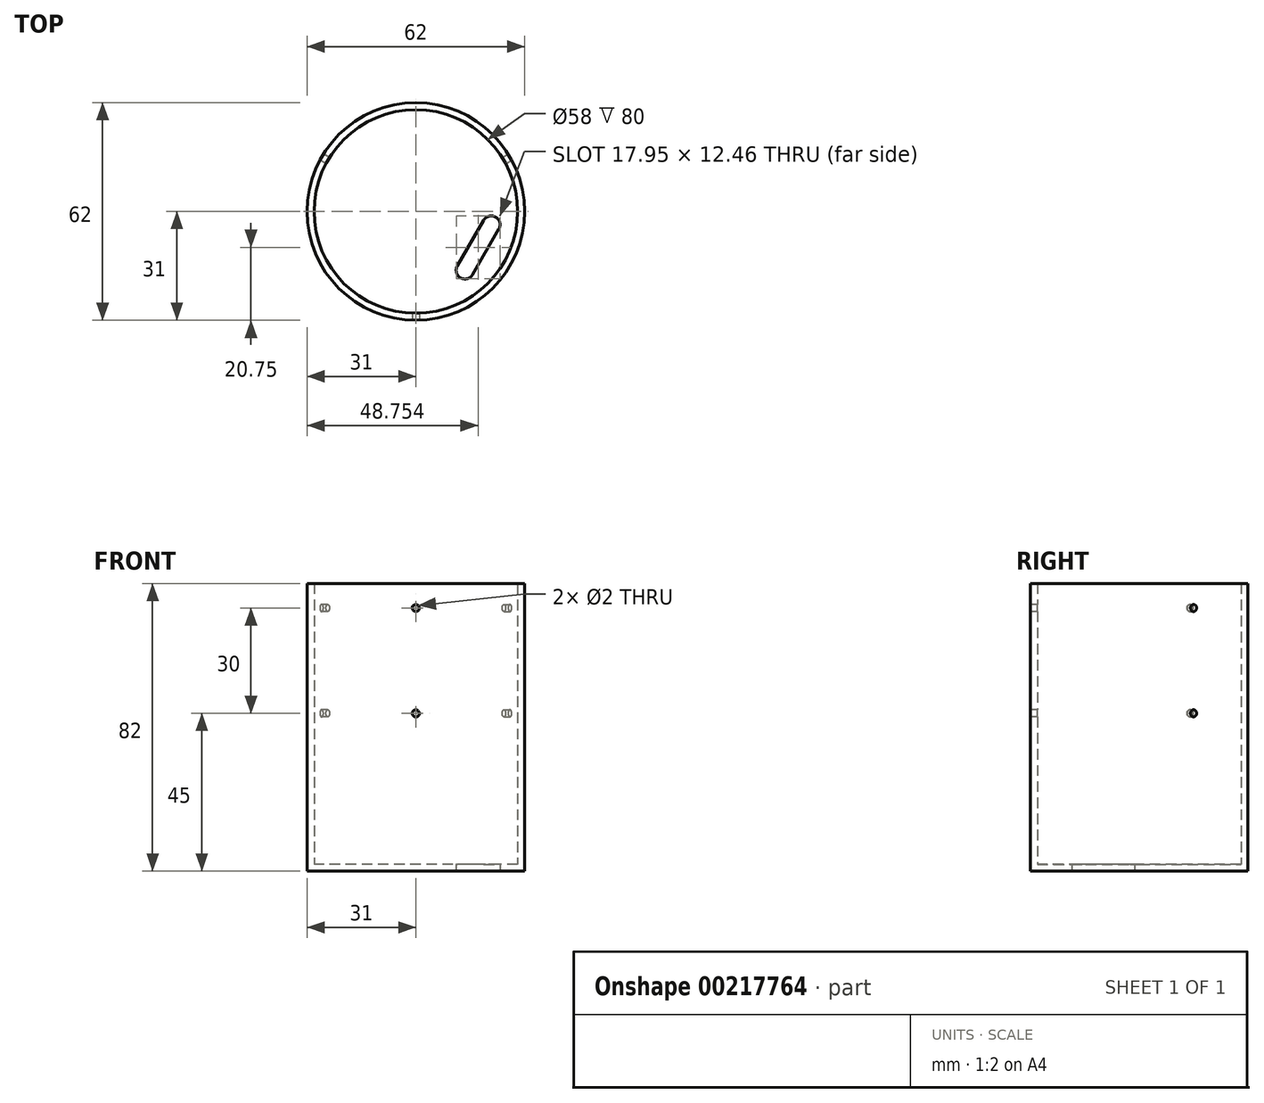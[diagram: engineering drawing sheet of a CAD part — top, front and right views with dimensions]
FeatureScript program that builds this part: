
annotation { "Feature Type Name" : "Feature", "Feature Type Description" : "" }
export const myFeature = defineFeature(function(context is Context, id is Id, definition is map)
    precondition{}
    {
        {
            var Q0;
            Q0=qCreatedBy(makeId("Top.planeOp"),FACE);
            var sketch = newSketch(context, id + "F0", { "sketchPlane" : qUnion([Q0])});
            skCircle(sketch, "E0", {"center": v(0, 0) * mm, "radius": 29 * mm});
            skCircle(sketch, "E1", {"center": v(0, 0) * mm, "radius": 31 * mm});
            skSolve(sketch);
        }
        {
            var Q0;
            Q0 = qSketchRegion(id + "F0", true);
            extrude(context, id + "F1", {"entities" : qUnion([Q0]), "depth" : 80 * mm});
        }
        {
            var Q0;
            Q0=qCreatedBy(makeId("Front.planeOp"),FACE);
            cPlane(context, id + "F2", {"entities" : qUnion([Q0]), "cplaneType" : CPlaneType.OFFSET, "offset" : 31 * mm, "width" : 150 * mm, "height" : 150 * mm});
        }
        {
            var Q0;
            Q0=qCreatedBy(id+"F2.planeOp",FACE);
            var sketch = newSketch(context, id + "F3", { "sketchPlane" : qUnion([Q0])});
            skLineSegment(sketch, "E2", {"start": v(0, 0) * mm, "end": v(0, 80) * mm, "construction": true});
            skCircle(sketch, "E3", {"center": v(0, 73) * mm, "radius": 1 * mm});
            skCircle(sketch, "E4", {"center": v(0, 43) * mm, "radius": 1 * mm});
            skSolve(sketch);
        }
        {
            var Q0;
            Q0 = qSketchRegion(id + "F3", true);
            extrude(context, id + "F4", {"entities" : qUnion([Q0]), "endBound" : BoundingType.UP_TO_NEXT, "oppositeDirection" : true, "depth" : 25 * mm});
        }
        {
            var Q0;
            Q0=makeQuery(id+"F4.opExtrude","SWEPT_BODY",BODY,{"disambiguationData":[OSD([sQuery(id+"F3.wireOp",EDGE,"E3")])]});
            var Q1;
            Q1=makeQuery(id+"F4.opExtrude","SWEPT_BODY",BODY,{"disambiguationData":[OSD([sQuery(id+"F3.wireOp",EDGE,"E4")])]});
            var Q2;
            Q2=makeQuery(id+"F1.opExtrude","CAP_EDGE",EDGE,{"disambiguationData":[OSD([sQuery(id+"F0.wireOp",EDGE,"E0")])],"isStart":false});
            circularPattern(context, id + "F5", {"entities" : qUnion([Q0, Q1]), "axis" : qUnion([Q2]), "angle" : 360 * degree, "instanceCount" : 3, "equalSpace" : true});
        }
        {
            var Q0;
            Q0=makeQuery(id+"F4.opExtrude","SWEPT_BODY",BODY,{"disambiguationData":[OSD([sQuery(id+"F3.wireOp",EDGE,"E3")])]});
            var Q1;
            Q1=makeQuery(id+"F4.opExtrude","SWEPT_BODY",BODY,{"disambiguationData":[OSD([sQuery(id+"F3.wireOp",EDGE,"E4")])]});
            var Q2;
            Q2=makeQuery(id+"F5.opPattern","COPY",BODY,{"derivedFrom":makeQuery(id+"F4.opExtrude","SWEPT_BODY",BODY,{"disambiguationData":[OSD([sQuery(id+"F3.wireOp",EDGE,"E3")])]}),"instanceName":"1"});
            var Q3;
            Q3=makeQuery(id+"F5.opPattern","COPY",BODY,{"derivedFrom":makeQuery(id+"F4.opExtrude","SWEPT_BODY",BODY,{"disambiguationData":[OSD([sQuery(id+"F3.wireOp",EDGE,"E4")])]}),"instanceName":"1"});
            var Q4;
            Q4=makeQuery(id+"F5.opPattern","COPY",BODY,{"derivedFrom":makeQuery(id+"F4.opExtrude","SWEPT_BODY",BODY,{"disambiguationData":[OSD([sQuery(id+"F3.wireOp",EDGE,"E3")])]}),"instanceName":"2"});
            var Q5;
            Q5=makeQuery(id+"F5.opPattern","COPY",BODY,{"derivedFrom":makeQuery(id+"F4.opExtrude","SWEPT_BODY",BODY,{"disambiguationData":[OSD([sQuery(id+"F3.wireOp",EDGE,"E4")])]}),"instanceName":"2"});
            var Q6;
            Q6=makeQuery(id+"F1.opExtrude","SWEPT_BODY",BODY,{"disambiguationData":[OSD([sQuery(id+"F0.wireOp",EDGE,"E0"),sQuery(id+"F0.wireOp",EDGE,"E1")])]});
            booleanBodies(context, id + "F6", {"operationType" : BooleanOperationType.SUBTRACTION, "tools" : qUnion([Q0, Q1, Q2, Q3, Q4, Q5]), "targets" : qUnion([Q6])});
        }
        {
            var Q0;
            Q0=makeQuery(id+"F1.opExtrude","CAP_FACE",FACE,{"disambiguationData":[OSD([sQuery(id+"F0.wireOp",EDGE,"E0"),sQuery(id+"F0.wireOp",EDGE,"E1")])],"isStart":true});
            var sketch = newSketch(context, id + "F7", { "sketchPlane" : qUnion([Q0])});
            skCircle(sketch, "E5", {"center": v(0, 0) * mm, "radius": 31 * mm});
            skSolve(sketch);
        }
        {
            var Q0;
            Q0 = qSketchRegion(id + "F7", true);
            extrude(context, id + "F8", {"entities" : qUnion([Q0]), "operationType" : NewBodyOperationType.ADD, "depth" : 2 * mm});
        }
        {
            var Q0;
            Q0=makeQuery(id+"F8.opExtrude","CAP_FACE",FACE,{"disambiguationData":[OSD([sQuery(id+"F7.wireOp",EDGE,"E5")])],"isStart":false});
            var sketch = newSketch(context, id + "F9", { "sketchPlane" : qUnion([Q0])});
            skLineSegment(sketch, "E6", {"start": v(11.84, 15.5) * mm, "end": v(19.34, 2.5) * mm});
            skLineSegment(sketch, "E7", {"start": v(16.17, 18) * mm, "end": v(23.67, 5) * mm});
            skArc(sketch, "E8", {"start": v(11.84, 15.5) * mm, "mid": v(12.75, 18.91) * mm, "end": v(16.17, 18) * mm});
            skArc(sketch, "E9", {"start": v(23.67, 5) * mm, "mid": v(22.75, 1.59) * mm, "end": v(19.34, 2.5) * mm});
            skLineSegment(sketch, "E10", {"start": v(0, 0) * mm, "end": v(26.85, 15.5) * mm, "construction": true});
            skLineSegment(sketch, "E11", {"start": v(0, 0) * mm, "end": v(0, 31) * mm, "construction": true});
            skPoint(sketch, "E12", {"position": v(15.59, 9) * mm});
            skPoint(sketch, "E13", {"position": v(19.92, 11.5) * mm});
            skSolve(sketch);
        }
        {
            var Q0;
            Q0 = qSketchRegion(id + "F9", true);
            extrude(context, id + "F10", {"entities" : qUnion([Q0]), "operationType" : NewBodyOperationType.REMOVE, "endBound" : BoundingType.UP_TO_NEXT, "oppositeDirection" : true, "depth" : 25 * mm});
        }
    });
